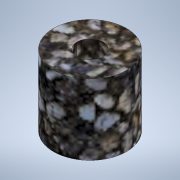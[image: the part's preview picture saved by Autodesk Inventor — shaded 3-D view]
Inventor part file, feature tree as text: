
AUTODESK INVENTOR PART (.ipt)
format: ipt  version: 2021 (Build 250183000, 183)  size: 135,168 bytes
history: native  units: mm
features: revolve x1, sketch x1
ambient origin geometry x8: Origin, YZ Plane, XZ Plane, XY Plane, X Axis, Y Axis, Z Axis, Center Point
bodies: Solid1 (feature_tree)
feature tree (2):
  revolve  "Revolution1"  [1 undecoded]
  sketch  "Sketch1"  dims[d0=5.5mm d1=15.5mm d2=30.0mm d3=90.0deg]
note: 1 required parameter value undecoded (feature->parameter linkage not recoverable at this tier; creation-order binding heuristic only, values carry confidence <= 0.55)
